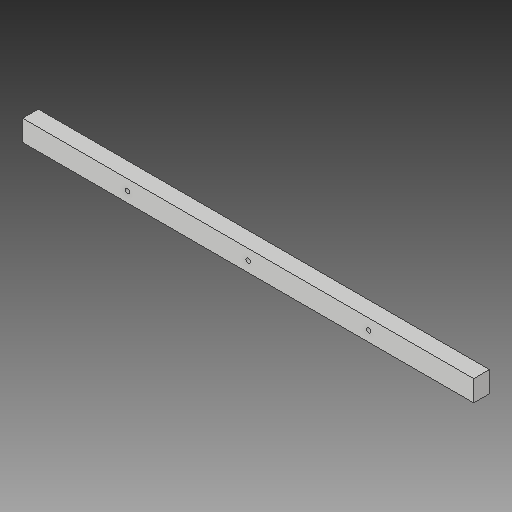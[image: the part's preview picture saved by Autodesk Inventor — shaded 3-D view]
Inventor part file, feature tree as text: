
AUTODESK INVENTOR PART (.ipt)
format: ipt  version: 2019 (Build 230136000, 136)  size: 98,816 bytes
history: native  units: in
note: dims shown in document units (in); Inventor stores cm internally (conversion verified against a paired STEP export)
features: extrude x2, sketch x2, other x2, reference x1, helix x1
ambient origin geometry x8: Origin, YZ Plane, XZ Plane, XY Plane, X Axis, Y Axis, Z Axis, Center Point
bodies: Solid1 (feature_tree)
feature tree (8):
  extrude  "Extrusion1"  Depth=0.5906in TaperAngle=0.0deg
  extrude  "Extrusion2"  Depth=16.9291in
  sketch  "Sketch1"  dims[d1=0.7874in d2=0.5906in d3=0.0in]
  reference  "Reference1"
  sketch  "Sketch2"  dims[d4=0.1654in d5=3.937in d6=0.1654in d7=3.937in d8=0.1654in d9=0.3937in d10=0.0in d11=16.9291in]
  other  "<userpath>\Documents\CAD Files\Helix DLP\Helix DLP.iam"
  helix  "Helix DLP.iam"  [1 undecoded]
  other  "Tank2:1"
note: 1 required parameter value undecoded (feature->parameter linkage not recoverable at this tier; creation-order binding heuristic only, values carry confidence <= 0.55)
